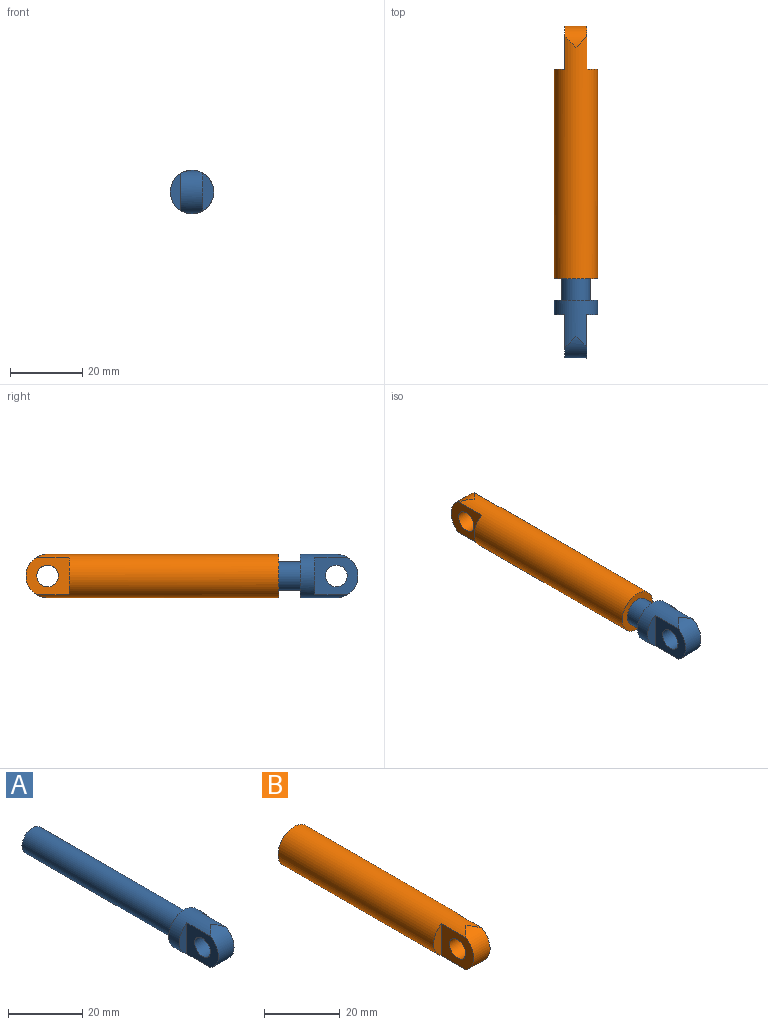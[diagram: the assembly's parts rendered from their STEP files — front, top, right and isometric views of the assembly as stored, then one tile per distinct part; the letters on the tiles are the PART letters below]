
ASSEMBLY  parts=2 mates=1
PART A: 10 faces, bbox 12x74x12 mm
  f0: cylinder r=6mm len=13.09mm, axis (0,1,0), area 245.5mm2, adj f1,f2,f3,f6,f7,f9
  f1: plane 12x10.29mm, normal (-1,0,0), area 86.5mm2, adj f0,f6,f8,f9
  f2: plane 12x10.49mm, normal (1,0,0), area 88.2mm2, adj f0,f3,f8,f9
  f3: plane 10.49x3.09mm, normal (0,-1,0), area 23mm2, adj f0,f2
  f4: cylinder r=4mm len=58mm, axis (0,1,0), area 1457.7mm2, adj f5,f7
  f5: plane 8x8mm, normal (0,1,0), area 50.3mm2, adj f4
  f6: plane 10.29x2.92mm, normal (0,-1,0), area 21.2mm2, adj f0,f1
  f7: plane 12x12mm, normal (0,1,0), area 62.8mm2, adj f0,f4
  f8: cylinder r=3mm len=6mm, axis (1,0,0), area 113.1mm2, adj f1,f2
  f9: cylinder r=6mm len=12mm, axis (1,0,0), area 94.7mm2, adj f0,f1,f2
PART B: 10 faces, bbox 12x70x12 mm
  f0: cylinder r=6mm len=67.05mm, axis (0,1,0), area 2283.3mm2, adj f1,f2,f3,f4,f7,f9
  f1: plane 12x10.34mm, normal (1,0,0), area 86.9mm2, adj f0,f2,f8,f9
  f2: plane 10.34x2.95mm, normal (0,-1,0), area 21.6mm2, adj f0,f1
  f3: plane 10.34x2.95mm, normal (0,-1,0), area 21.6mm2, adj f0,f7
  f4: plane 12x12mm, normal (0,1,0), area 62.8mm2, adj f0,f5
  f5: cylinder r=4mm len=56mm, axis (0,1,0), area 1407.4mm2, adj f4,f6
  f6: plane 8x8mm, normal (0,1,0), area 50.3mm2, adj f5
  f7: plane 12x10.34mm, normal (-1,0,0), area 86.9mm2, adj f0,f3,f8,f9
  f8: cylinder r=3mm len=6.1mm, axis (-1,0,0), area 114.9mm2, adj f1,f7
  f9: cylinder r=6mm len=12mm, axis (-1,0,0), area 95.9mm2, adj f0,f1,f7
PLACE A t=(-6.98,-7.78,-8.14)mm
PLACE B rot(axis=(1,0,0),180deg) t=(-6.98,-59.78,-8.14)mm
MATE slider B.f0 <-> A.f4  axis (0,-1,0) through (-6.98,-31.78,-8.14)mm
